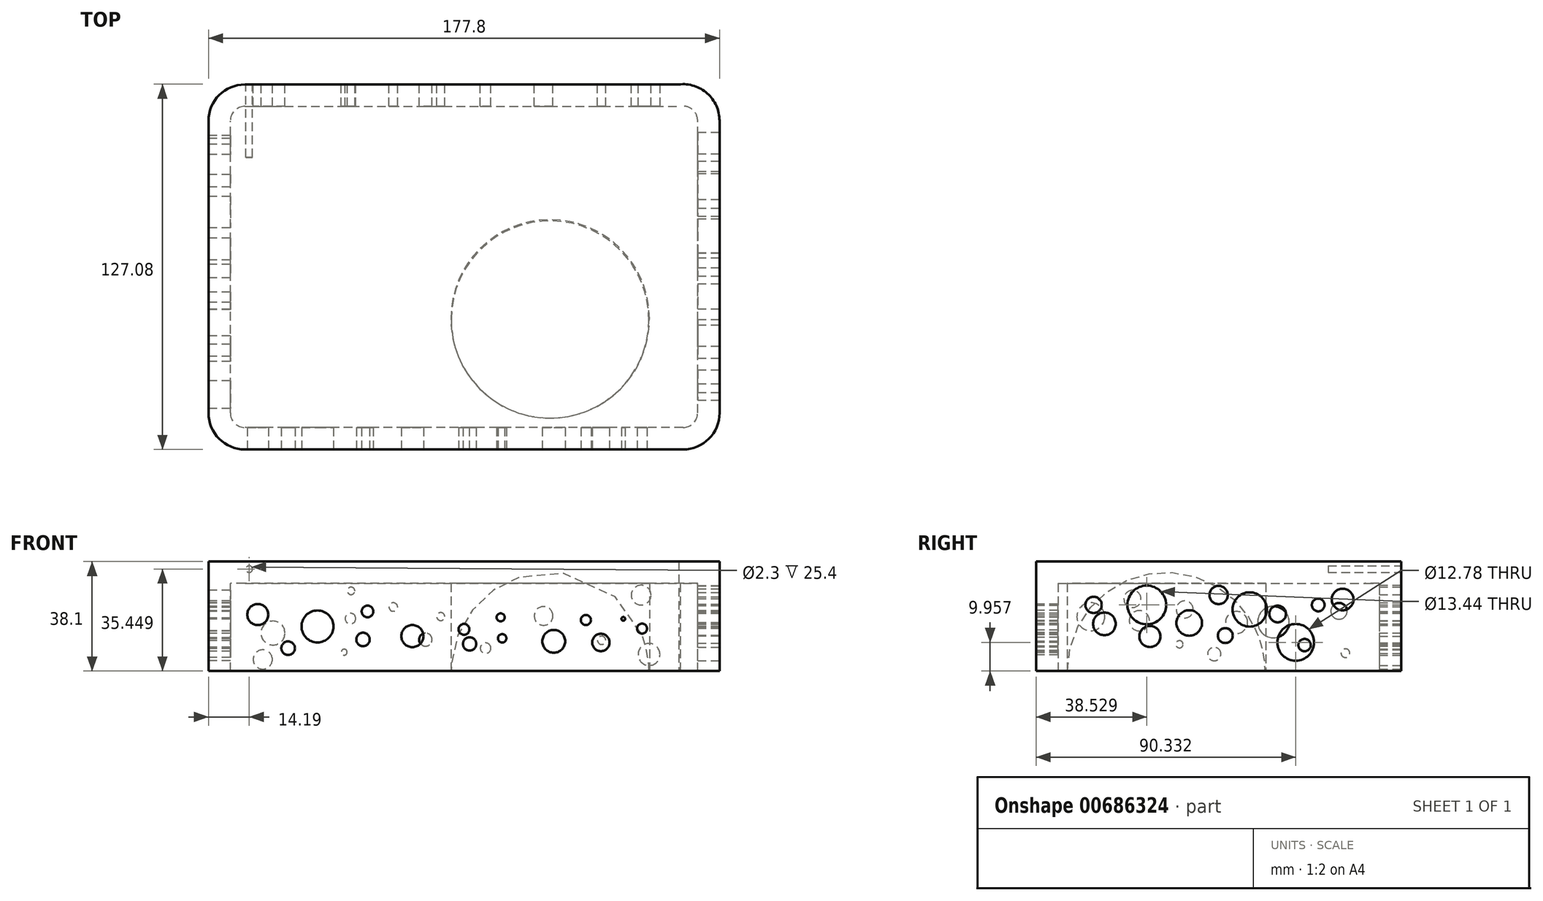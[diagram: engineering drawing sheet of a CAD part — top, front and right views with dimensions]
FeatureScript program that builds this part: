
annotation { "Feature Type Name" : "Feature", "Feature Type Description" : "" }
export const myFeature = defineFeature(function(context is Context, id is Id, definition is map)
    precondition{}
    {
        {
            var Q0;
            Q0=qCreatedBy(makeId("Top.planeOp"),FACE);
            var sketch = newSketch(context, id + "F0", { "sketchPlane" : qUnion([Q0])});
            skLineSegment(sketch, "E0.bottom", {"start": v(76.2, -63.5) * mm, "end": v(-76.2, -63.5) * mm});
            skLineSegment(sketch, "E0.left", {"start": v(88.9, -50.8) * mm, "end": v(88.9, 50.88) * mm});
            skLineSegment(sketch, "E0.right", {"start": v(-88.9, -50.8) * mm, "end": v(-88.9, 50.8) * mm});
            skPoint(sketch, "E0.middle", {"position": v(0, 0) * mm});
            skPoint(sketch, "E1.visualSharp", {"position": v(-88.9, 63.5) * mm});
            skArc(sketch, "E1.filletArc", {"start": v(-76.2, 63.5) * mm, "mid": v(-85.18, 59.78) * mm, "end": v(-88.9, 50.8) * mm});
            skPoint(sketch, "E2.visualSharp", {"position": v(-88.9, -63.5) * mm});
            skArc(sketch, "E2.filletArc", {"start": v(-88.9, -50.8) * mm, "mid": v(-85.18, -59.78) * mm, "end": v(-76.2, -63.5) * mm});
            skPoint(sketch, "E3.visualSharp", {"position": v(88.9, -63.5) * mm});
            skArc(sketch, "E3.filletArc", {"start": v(76.2, -63.5) * mm, "mid": v(85.18, -59.78) * mm, "end": v(88.9, -50.8) * mm});
            skPoint(sketch, "E4.visualSharp", {"position": v(88.9, 63.5) * mm});
            skArc(sketch, "E4.filletArc", {"start": v(88.9, 50.88) * mm, "mid": v(84.65, 60.36) * mm, "end": v(74.74, 63.5) * mm});
            skLineSegment(sketch, "E5", {"start": v(-76.2, 63.5) * mm, "end": v(-51.82, 63.5) * mm});
            skLineSegment(sketch, "E6", {"start": v(-31.5, 63.5) * mm, "end": v(74.74, 63.5) * mm});
            skLineSegment(sketch, "E7", {"start": v(-51.82, 63.5) * mm, "end": v(-31.5, 63.5) * mm});
            skLineSegment(sketch, "E8", {"start": v(-4.56, -17.2) * mm, "end": v(64.5, -17.2) * mm});
            skArc(sketch, "E9", {"start": v(-4.56, -17.2) * mm, "mid": v(29.97, -52.61) * mm, "end": v(64.5, -17.2) * mm});
            skArc(sketch, "E10", {"start": v(64.5, -17.2) * mm, "mid": v(29.97, 16.47) * mm, "end": v(-4.56, -17.2) * mm});
            skSolve(sketch);
        }
        {
            var Q0;
            Q0=makeQuery(id+"F0.imprint","IMPRINT",FACE,{"disambiguationData":[TD([[makeQuery(id+"F0.imprint","IMPRINT",EDGE,{"derivedFrom":sQuery(id+"F0.wireOp",EDGE,"E0.bottom")}),-1.0]])]});
            var Q1;
            Q1=makeQuery(id+"F0.imprint","IMPRINT",FACE,{"disambiguationData":[TD([[makeQuery(id+"F0.imprint","IMPRINT",EDGE,{"derivedFrom":sQuery(id+"F0.wireOp",EDGE,"OtEaktRJ-8dN9-yVeX-Mm1L-FsvAlRXxjRDO")}),1.0]])]});
            var Q2;
            Q2=makeQuery(id+"F0.imprint","IMPRINT",FACE,{"disambiguationData":[TD([[makeQuery(id+"F0.imprint","IMPRINT",EDGE,{"derivedFrom":sQuery(id+"F0.wireOp",EDGE,"E8")}),1.0]])]});
            var Q3;
            Q3=makeQuery(id+"F0.imprint","IMPRINT",FACE,{"disambiguationData":[TD([[makeQuery(id+"F0.imprint","IMPRINT",EDGE,{"derivedFrom":sQuery(id+"F0.wireOp",EDGE,"E8")}),-1.0]])]});
            extrude(context, id + "F1", {"entities" : qUnion([Q0, Q1, Q2, Q3]), "depth" : 38.1 * mm, "offsetDistance" : 25.4 * mm});
        }
        {
            var Q0;
            Q0=makeQuery(id+"F1.opExtrude","SWEPT_FACE",FACE,{"disambiguationData":[OSD([sQuery(id+"F0.wireOp",EDGE,"E0.bottom")])]});
            var sketch = newSketch(context, id + "F2", { "sketchPlane" : qUnion([Q0])});
            skPoint(sketch, "E11", {"position": v(-63.57, 0) * mm});
            skPoint(sketch, "E12", {"position": v(-45.35, 0) * mm});
            skPoint(sketch, "E13", {"position": v(-11.93, 0) * mm});
            skPoint(sketch, "E14", {"position": v(25.4, 0) * mm});
            skPoint(sketch, "E15", {"position": v(60.4, 0) * mm});
            skPoint(sketch, "E16", {"position": v(49.8, 0) * mm});
            skCircle(sketch, "E17", {"center": v(-63.57, 0) * mm, "radius": 2.88 * mm});
            skCircle(sketch, "E18", {"center": v(-45.35, 0) * mm, "radius": 5.96 * mm});
            skCircle(sketch, "E19", {"center": v(-11.93, 0) * mm, "radius": 4.96 * mm});
            skCircle(sketch, "E20", {"center": v(25.4, 0) * mm, "radius": 4.39 * mm});
            skCircle(sketch, "E21", {"center": v(49.8, 0) * mm, "radius": 3.38 * mm});
            skCircle(sketch, "E22", {"center": v(60.4, 0) * mm, "radius": 3.13 * mm});
            skSolve(sketch);
        }
        {
            var Q0;
            Q0=makeQuery(id+"F1.opExtrude","SWEPT_FACE",FACE,{"disambiguationData":[OSD([sQuery(id+"F0.wireOp",EDGE,"E0.right")])]});
            var sketch = newSketch(context, id + "F3", { "sketchPlane" : qUnion([Q0])});
            skPoint(sketch, "E23", {"position": v(-39.41, 0) * mm});
            skPoint(sketch, "E24", {"position": v(-28.41, 0) * mm});
            skPoint(sketch, "E25", {"position": v(-23.86, 0) * mm});
            skPoint(sketch, "E26", {"position": v(-8.19, 0) * mm});
            skPoint(sketch, "E27", {"position": v(9, 0) * mm});
            skPoint(sketch, "E28", {"position": v(27.2, 0) * mm});
            skPoint(sketch, "E29", {"position": v(44.14, 0) * mm});
            skCircle(sketch, "E30", {"center": v(-39.41, 0) * mm, "radius": 2.01 * mm});
            skCircle(sketch, "E31", {"center": v(-28.41, 0) * mm, "radius": 2.58 * mm});
            skCircle(sketch, "E32", {"center": v(-23.86, 0) * mm, "radius": 1.22 * mm});
            skCircle(sketch, "E33", {"center": v(-8.19, 0) * mm, "radius": 2.72 * mm});
            skCircle(sketch, "E34", {"center": v(9, 0) * mm, "radius": 1.99 * mm});
            skCircle(sketch, "E35", {"center": v(27.2, 0) * mm, "radius": 3.6 * mm});
            skCircle(sketch, "E36", {"center": v(44.14, 0) * mm, "radius": 0.95 * mm});
            skSolve(sketch);
        }
        {
            var Q0;
            Q0=makeQuery(id+"F1.opExtrude","SWEPT_FACE",FACE,{"disambiguationData":[OSD([sQuery(id+"F0.wireOp",EDGE,"E5"),sQuery(id+"F0.wireOp",EDGE,"E6"),sQuery(id+"F0.wireOp",EDGE,"E7")])]});
            var sketch = newSketch(context, id + "F4", { "sketchPlane" : qUnion([Q0])});
            skPoint(sketch, "E37", {"position": v(-56.6, 0) * mm});
            skPoint(sketch, "E38", {"position": v(-45.12, 0) * mm});
            skPoint(sketch, "E39", {"position": v(-30.45, 0) * mm});
            skPoint(sketch, "E40", {"position": v(-1.78, -0.93) * mm});
            skPoint(sketch, "E41", {"position": v(-4.3, 0) * mm});
            skPoint(sketch, "E42", {"position": v(15.08, 0) * mm});
            skPoint(sketch, "E43", {"position": v(30.68, 0) * mm});
            skPoint(sketch, "E44", {"position": v(53.5, 0) * mm});
            skCircle(sketch, "E45", {"center": v(-56.6, 0) * mm, "radius": 2.44 * mm});
            skCircle(sketch, "E46", {"center": v(-45.12, 0) * mm, "radius": 2.44 * mm});
            skCircle(sketch, "E47", {"center": v(-30.45, 0) * mm, "radius": 3.8 * mm});
            skCircle(sketch, "E48", {"center": v(-3.38, 0) * mm, "radius": 3.87 * mm});
            skCircle(sketch, "E49", {"center": v(15.08, 0) * mm, "radius": 1.49 * mm});
            skCircle(sketch, "E50", {"center": v(30.68, 0) * mm, "radius": 1.53 * mm});
            skCircle(sketch, "E51", {"center": v(53.5, 0) * mm, "radius": 3.37 * mm});
            skSolve(sketch);
        }
        {
            var Q0;
            Q0=makeQuery(id+"F1.opExtrude","SWEPT_FACE",FACE,{"disambiguationData":[OSD([sQuery(id+"F0.wireOp",EDGE,"E0.left")])]});
            var sketch = newSketch(context, id + "F5", { "sketchPlane" : qUnion([Q0])});
            skPoint(sketch, "E52", {"position": v(-34.1, 0) * mm});
            skPoint(sketch, "E53", {"position": v(-25.82, 0) * mm});
            skPoint(sketch, "E54", {"position": v(-12.79, 0.83) * mm});
            skPoint(sketch, "E55", {"position": v(-10.57, 0) * mm});
            skPoint(sketch, "E56", {"position": v(20.4, 0.83) * mm});
            skPoint(sketch, "E57", {"position": v(23.52, 0) * mm});
            skCircle(sketch, "E58", {"center": v(-34.1, 0) * mm, "radius": 0.86 * mm});
            skCircle(sketch, "E59", {"center": v(-25.24, 0) * mm, "radius": 1.05 * mm});
            skCircle(sketch, "E60", {"center": v(-10.57, 0) * mm, "radius": 2.08 * mm});
            skCircle(sketch, "E61", {"center": v(23.52, 0) * mm, "radius": 3.61 * mm});
            skSolve(sketch);
        }
        {
            var Q0;
            Q0=makeQuery(id+"F1.opExtrude","CAP_FACE",FACE,{"disambiguationData":[OSD([sQuery(id+"F0.wireOp",EDGE,"E0.bottom"),sQuery(id+"F0.wireOp",EDGE,"E0.left"),sQuery(id+"F0.wireOp",EDGE,"E0.right"),sQuery(id+"F0.wireOp",EDGE,"E1.filletArc"),sQuery(id+"F0.wireOp",EDGE,"E2.filletArc"),sQuery(id+"F0.wireOp",EDGE,"E3.filletArc"),sQuery(id+"F0.wireOp",EDGE,"E4.filletArc"),sQuery(id+"F0.wireOp",EDGE,"E5"),sQuery(id+"F0.wireOp",EDGE,"E6"),sQuery(id+"F0.wireOp",EDGE,"E7")])],"isStart":true});
            shell(context, id + "F6", {"entities" : qUnion([Q0]), "thickness" : 7.62 * mm});
        }
        {
            var Q0;
            Q0=makeQuery(id+"F0.imprint","IMPRINT",FACE,{"disambiguationData":[TD([[makeQuery(id+"F0.imprint","IMPRINT",EDGE,{"derivedFrom":sQuery(id+"F0.wireOp",EDGE,"E8")}),-1.0]])]});
            var Q1;
            Q1=makeQuery(id+"F0.imprint","IMPRINT",FACE,{"disambiguationData":[TD([[makeQuery(id+"F0.imprint","IMPRINT",EDGE,{"derivedFrom":sQuery(id+"F0.wireOp",EDGE,"E8")}),1.0]])]});
            extrude(context, id + "F7", {"entities" : qUnion([Q0, Q1]), "operationType" : NewBodyOperationType.ADD, "depth" : 38.1 * mm, "offsetDistance" : 25.4 * mm});
        }
        {
            var Q0;
            Q0=makeQuery(id+"F0.imprint","IMPRINT",FACE,{"disambiguationData":[TD([[makeQuery(id+"F0.imprint","IMPRINT",EDGE,{"derivedFrom":sQuery(id+"F0.wireOp",EDGE,"E8")}),-1.0]])]});
            var sketch = newSketch(context, id + "F8", { "sketchPlane" : qUnion([Q0])});
            skLineSegment(sketch, "E62", {"start": v(-4.45, -17.67) * mm, "end": v(64.33, -18.9) * mm});
            skArc(sketch, "E63", {"start": v(-4.45, -17.67) * mm, "mid": v(29.32, -52.6) * mm, "end": v(64.33, -18.9) * mm});
            skArc(sketch, "E64", {"start": v(64.33, -18.9) * mm, "mid": v(30.56, 16.18) * mm, "end": v(-4.45, -17.67) * mm});
            skSolve(sketch);
        }
        {
            var Q0;
            Q0=makeQuery(id+"F8.imprint","IMPRINT",FACE,{"disambiguationData":[TD([[makeQuery(id+"F8.imprint","IMPRINT",EDGE,{"derivedFrom":sQuery(id+"F8.wireOp",EDGE,"E62")}),-1.0]])]});
            var Q1;
            Q1=sQuery(id+"F8.wireOp",EDGE,"E62");
            revolve(context, id + "F9", {"operationType" : NewBodyOperationType.REMOVE, "entities" : qUnion([Q0]), "axis" : qUnion([Q1]), "revolveType" : RevolveType.FULL, "oppositeDirection" : true});
        }
        {
            var Q0;
            {var subQ2=sQuery(id+"F0.wireOp",EDGE,"E5");var subQ3=makeQuery(id+"F1.opExtrude","SWEPT_EDGE",EDGE,{"disambiguationData":[OSD([sQuery(id+"F0.wireOp",EDGE,"E1.filletArc"),subQ2])]});Q0=makeQuery(id+"F4.imprint","IMPRINT",FACE,{"disambiguationData":[TD([[makeQuery(id+"F4.imprint","IMPRINT",EDGE,{"derivedFrom":subQ3}),-1.0]])]});}
            var sketch = newSketch(context, id + "F10", { "sketchPlane" : qUnion([Q0])});
            skPoint(sketch, "E65", {"position": v(-27.7, 19.16) * mm});
            skPoint(sketch, "E66", {"position": v(-47.88, 10.68) * mm});
            skPoint(sketch, "E67", {"position": v(-61.64, 26.39) * mm});
            skPoint(sketch, "E68", {"position": v(15.88, 25.47) * mm});
            skPoint(sketch, "E69", {"position": v(24.6, 14.8) * mm});
            skPoint(sketch, "E70", {"position": v(-4.76, 11.83) * mm});
            skPoint(sketch, "E71", {"position": v(48, 21.92) * mm});
            skPoint(sketch, "E72", {"position": v(65.65, 29.72) * mm});
            skPoint(sketch, "E73", {"position": v(69.55, 15.95) * mm});
            skPoint(sketch, "E74", {"position": v(51.66, 9.76) * mm});
            skPoint(sketch, "E75", {"position": v(-32.62, 30.17) * mm});
            skCircle(sketch, "E76", {"center": v(-61.64, 26.39) * mm, "radius": 3.44 * mm});
            skCircle(sketch, "E77", {"center": v(-47.88, 10.68) * mm, "radius": 1.45 * mm});
            skCircle(sketch, "E78", {"center": v(-27.7, 19.16) * mm, "radius": 3.26 * mm});
            skCircle(sketch, "E79", {"center": v(8.08, 18.94) * mm, "radius": 1.4 * mm});
            skCircle(sketch, "E80", {"center": v(13.36, 10.9) * mm, "radius": 2.26 * mm});
            skCircle(sketch, "E81", {"center": v(-7.51, 7.93) * mm, "radius": 1.84 * mm});
            skCircle(sketch, "E82", {"center": v(24.6, 22.26) * mm, "radius": 1.5 * mm});
            skCircle(sketch, "E83", {"center": v(39.28, 27.88) * mm, "radius": 1.3 * mm});
            skCircle(sketch, "E84", {"center": v(39.5, 18.25) * mm, "radius": 1.84 * mm});
            skCircle(sketch, "E85", {"center": v(41.68, 6.55) * mm, "radius": 1.03 * mm});
            skCircle(sketch, "E86", {"center": v(-64.39, 5.75) * mm, "radius": 3.81 * mm});
            skCircle(sketch, "E87", {"center": v(66.45, 13.2) * mm, "radius": 4.17 * mm});
            skCircle(sketch, "E88", {"center": v(74.71, 35.45) * mm, "radius": 1.15 * mm});
            skCircle(sketch, "E89", {"center": v(70, 4.03) * mm, "radius": 3.34 * mm});
            skSolve(sketch);
        }
        {
            var Q0;
            Q0=qSketchRegion(id+"F10",true);
            extrude(context, id + "F11", {"entities" : qUnion([Q0]), "operationType" : NewBodyOperationType.REMOVE, "oppositeDirection" : true, "depth" : 25.4 * mm, "offsetDistance" : 25.4 * mm});
        }
        {
            var Q0;
            {var subQ0=sQuery(id+"F0.wireOp",EDGE,"E0.bottom");Q0=makeQuery(id+"F2.imprint","IMPRINT",FACE,{"disambiguationData":[TD([[makeQuery(id+"F2.imprint","IMPRINT",EDGE,{"derivedFrom":makeQuery(id+"F1.opExtrude","CAP_EDGE",EDGE,{"disambiguationData":[OSD([subQ0])],"isStart":false})}),1.0]])]});}
            var sketch = newSketch(context, id + "F12", { "sketchPlane" : qUnion([Q0])});
            skCircle(sketch, "E90", {"center": v(-71.73, 19.62) * mm, "radius": 3.66 * mm});
            skCircle(sketch, "E91", {"center": v(-61.18, 7.93) * mm, "radius": 2.36 * mm});
            skCircle(sketch, "E92", {"center": v(-50.97, 15.5) * mm, "radius": 5.55 * mm});
            skCircle(sketch, "E93", {"center": v(-33.57, 20.74) * mm, "radius": 2.03 * mm});
            skCircle(sketch, "E94", {"center": v(-35.13, 10.98) * mm, "radius": 2.35 * mm});
            skCircle(sketch, "E95", {"center": v(-17.96, 12.15) * mm, "radius": 3.84 * mm});
            skCircle(sketch, "E96", {"center": v(0, 14.49) * mm, "radius": 1.9 * mm});
            skCircle(sketch, "E97", {"center": v(12.75, 18.65) * mm, "radius": 1.4 * mm});
            skCircle(sketch, "E98", {"center": v(13.27, 11.37) * mm, "radius": 1.47 * mm});
            skCircle(sketch, "E99", {"center": v(1.95, 9.41) * mm, "radius": 2.3 * mm});
            skCircle(sketch, "E100", {"center": v(42.42, 17.74) * mm, "radius": 1.77 * mm});
            skCircle(sketch, "E101", {"center": v(55.43, 18.13) * mm, "radius": 0.65 * mm});
            skCircle(sketch, "E102", {"center": v(61.94, 14.75) * mm, "radius": 1.75 * mm});
            skCircle(sketch, "E103", {"center": v(47.63, 9.93) * mm, "radius": 3.02 * mm});
            skCircle(sketch, "E104", {"center": v(31.23, 10.32) * mm, "radius": 3.97 * mm});
            skSolve(sketch);
        }
        {
            var Q0;
            Q0=qSketchRegion(id+"F12",true);
            extrude(context, id + "F13", {"entities" : qUnion([Q0]), "operationType" : NewBodyOperationType.REMOVE, "oppositeDirection" : true, "depth" : 7.87 * mm, "offsetDistance" : 25.4 * mm});
        }
        {
            var Q0;
            {var subQ0=sQuery(id+"F0.wireOp",EDGE,"E0.right");Q0=makeQuery(id+"F3.imprint","IMPRINT",FACE,{"disambiguationData":[TD([[makeQuery(id+"F3.imprint","IMPRINT",EDGE,{"derivedFrom":makeQuery(id+"F1.opExtrude","CAP_EDGE",EDGE,{"disambiguationData":[OSD([subQ0])],"isStart":false})}),1.0]])]});}
            var sketch = newSketch(context, id + "F14", { "sketchPlane" : qUnion([Q0])});
            skCircle(sketch, "E105", {"center": v(-41.9, 20.84) * mm, "radius": 2.83 * mm});
            skCircle(sketch, "E106", {"center": v(-19.08, 17.03) * mm, "radius": 5.5 * mm});
            skCircle(sketch, "E107", {"center": v(11.77, 21.4) * mm, "radius": 2.96 * mm});
            skCircle(sketch, "E108", {"center": v(27.55, 17.45) * mm, "radius": 3.53 * mm});
            skCircle(sketch, "E109", {"center": v(44.45, 18.86) * mm, "radius": 4.87 * mm});
            skCircle(sketch, "E110", {"center": v(29.94, 25.06) * mm, "radius": 2.99 * mm});
            skCircle(sketch, "E111", {"center": v(13.6, 9.28) * mm, "radius": 1.26 * mm});
            skCircle(sketch, "E112", {"center": v(1.49, 5.9) * mm, "radius": 2.32 * mm});
            skCircle(sketch, "E113", {"center": v(-6.26, 16.9) * mm, "radius": 3.83 * mm});
            skCircle(sketch, "E114", {"center": v(-29.93, 9) * mm, "radius": 2.15 * mm});
            skCircle(sketch, "E115", {"center": v(-44.15, 6.18) * mm, "radius": 1.52 * mm});
            skSolve(sketch);
        }
        {
            var Q0;
            Q0=qSketchRegion(id+"F14",true);
            extrude(context, id + "F15", {"entities" : qUnion([Q0]), "operationType" : NewBodyOperationType.REMOVE, "oppositeDirection" : true, "depth" : 25.4 * mm, "offsetDistance" : 25.4 * mm});
        }
        {
            var Q0;
            {var subQ0=sQuery(id+"F0.wireOp",EDGE,"E0.left");Q0=makeQuery(id+"F5.imprint","IMPRINT",FACE,{"disambiguationData":[TD([[makeQuery(id+"F5.imprint","IMPRINT",EDGE,{"derivedFrom":makeQuery(id+"F1.opExtrude","CAP_EDGE",EDGE,{"disambiguationData":[OSD([subQ0])],"isStart":false})}),-1.0]])]});}
            var sketch = newSketch(context, id + "F16", { "sketchPlane" : qUnion([Q0])});
            skCircle(sketch, "E116", {"center": v(-43.5, 22.99) * mm, "radius": 2.84 * mm});
            skCircle(sketch, "E117", {"center": v(-24.97, 22.99) * mm, "radius": 6.72 * mm});
            skCircle(sketch, "E118", {"center": v(-39.73, 16.4) * mm, "radius": 3.93 * mm});
            skCircle(sketch, "E119", {"center": v(-23.87, 12) * mm, "radius": 3.66 * mm});
            skCircle(sketch, "E120", {"center": v(2.34, 12.31) * mm, "radius": 2.59 * mm});
            skCircle(sketch, "E121", {"center": v(20.55, 19.85) * mm, "radius": 2.9 * mm});
            skCircle(sketch, "E122", {"center": v(34.68, 22.99) * mm, "radius": 2.22 * mm});
            skCircle(sketch, "E123", {"center": v(43.16, 24.87) * mm, "radius": 3.77 * mm});
            skCircle(sketch, "E124", {"center": v(26.83, 9.96) * mm, "radius": 6.4 * mm});
            skCircle(sketch, "E125", {"center": v(0, 26.44) * mm, "radius": 3.18 * mm});
            skCircle(sketch, "E126", {"center": v(-10.21, 16.7) * mm, "radius": 4.44 * mm});
            skCircle(sketch, "E127", {"center": v(10.82, 21.42) * mm, "radius": 5.97 * mm});
            skSolve(sketch);
        }
        {
            var Q0;
            Q0=qSketchRegion(id+"F16",true);
            extrude(context, id + "F17", {"entities" : qUnion([Q0]), "operationType" : NewBodyOperationType.REMOVE, "oppositeDirection" : true, "depth" : 7.62 * mm, "offsetDistance" : 25.4 * mm});
        }
    });
